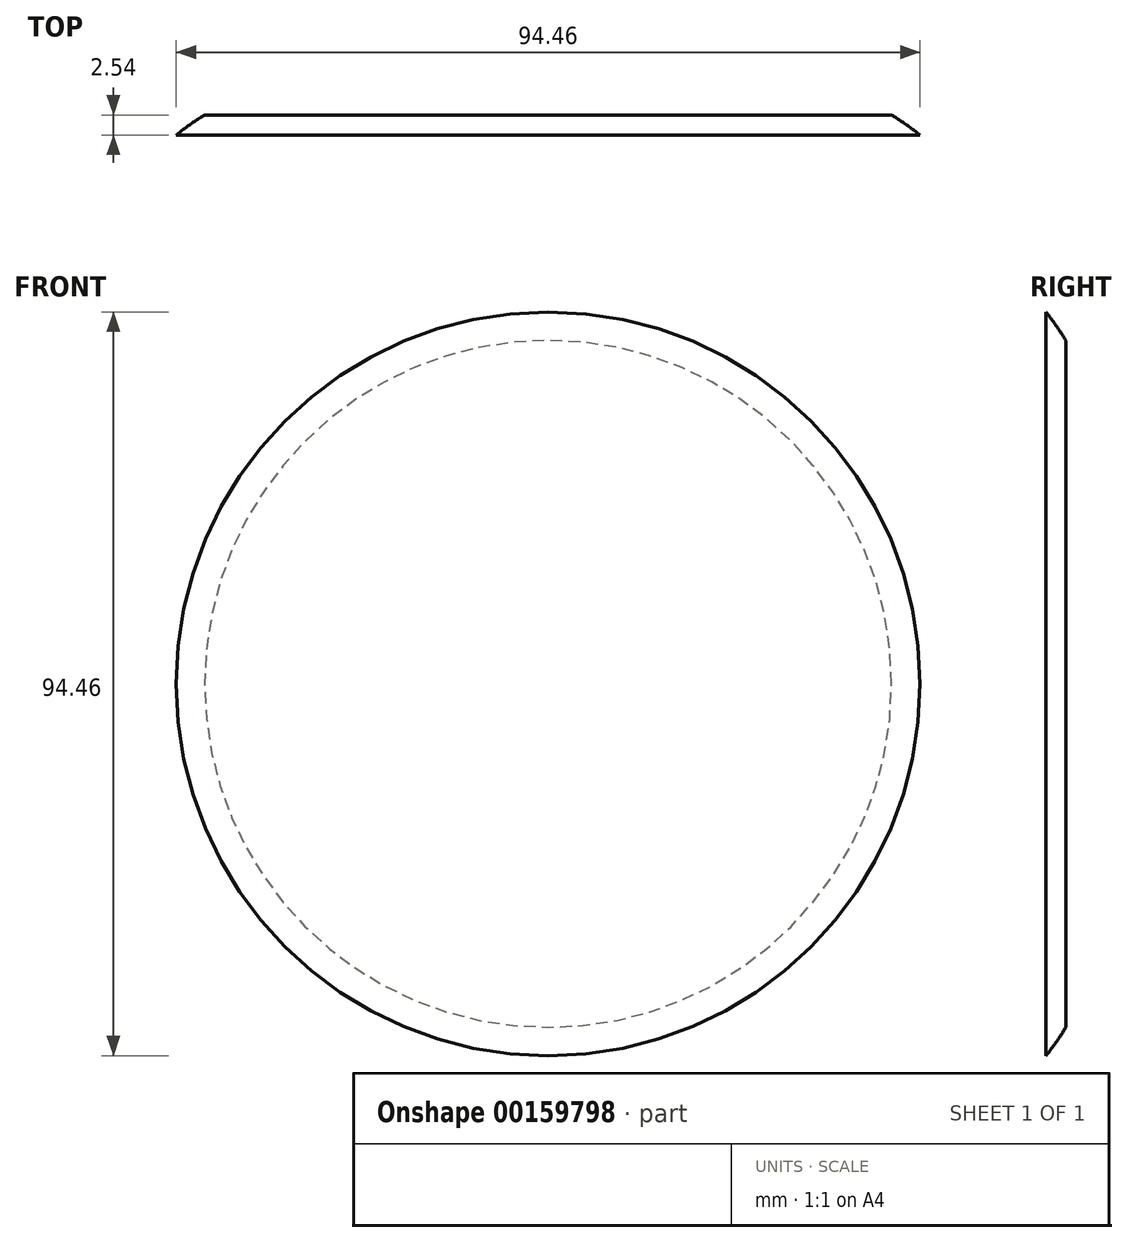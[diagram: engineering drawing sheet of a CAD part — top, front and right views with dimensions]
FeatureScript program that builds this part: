
annotation { "Feature Type Name" : "Feature", "Feature Type Description" : "" }
export const myFeature = defineFeature(function(context is Context, id is Id, definition is map)
    precondition{}
    {
        {
            var Q0;
            Q0=qCreatedBy(makeId("Top.planeOp"),FACE);
            var sketch = newSketch(context, id + "F0", { "sketchPlane" : qUnion([Q0])});
            skFitSpline(sketch, "E0", {"points": [v(-112.61, -64.12) * mm, v(-122.22, -64.33) * mm, v(-136.96, -65.83) * mm, v(-154.68, -71.66) * mm, v(-168.67, -85.12) * mm, v(-178.98, -107.06) * mm, v(-180.56, -121.57) * mm, v(-177.12, -143.23) * mm, v(-165.25, -161.2) * mm, v(-152.56, -172.55) * mm, v(-134.87, -180.47) * mm, v(-112.66, -180.75) * mm], "startDerivative": vector(0, -220.05) * mm, "endDerivative": vector(374.48, 15.9) * mm});
            skFitSpline(sketch, "E1", {"points": [v(-112.66, -66.89) * mm, v(-121.93, -72.44) * mm, v(-134.08, -72.96) * mm, v(-148.87, -75.08) * mm, v(-160.5, -86.97) * mm, v(-170.8, -107.3) * mm, v(-172.65, -121.84) * mm, v(-168.16, -141.39) * mm, v(-159.44, -156.97) * mm, v(-139.1, -173.35) * mm, v(-112.66, -176.26) * mm], "startDerivative": vector(-52.26, -120.91) * mm, "endDerivative": vector(225.03, 5.6) * mm});
            skLineSegment(sketch, "E2", {"start": v(-184.97, -75.08) * mm, "end": v(0, -75.08) * mm});
            skLineSegment(sketch, "E3", {"start": v(-112.61, -19) * mm, "end": v(-112.61, -203.86) * mm});
            skFitSpline(sketch, "E4", {"points": [v(-112.61, -64.12) * mm, v(-111.12, -57.31) * mm, v(-104.07, -38.9) * mm, v(-98.3, -26.81) * mm], "startDerivative": vector(3.84, 23.75) * mm, "endDerivative": vector(16.05, 31.9) * mm});
            skSolve(sketch);
        }
        {
            var Q0;
            {var subQ0=sQuery(id+"F0.wireOp",EDGE,"E0");Q0=makeQuery(id+"F0.imprint","IMPRINT",FACE,{"disambiguationData":[TD([[makeQuery(id+"F0.imprint","IMPRINT",EDGE,{"derivedFrom":subQ0}),1.0]])]});}
            var Q1;
            Q1=sQuery(id+"F0.wireOp",EDGE,"E3");
            revolve(context, id + "F1", {"entities" : qUnion([Q0]), "axis" : qUnion([Q1]), "revolveType" : RevolveType.FULL});
        }
        {
            var Q0;
            Q0=makeQuery(id+"F1.opRevolve","SWEPT_FACE",FACE,{"disambiguationData":[OSD([sQuery(id+"F0.wireOp",EDGE,"E0")])]});
            shell(context, id + "F2", {"entities" : qUnion([Q0]), "thickness" : 2.54 * mm});
        }
    });
